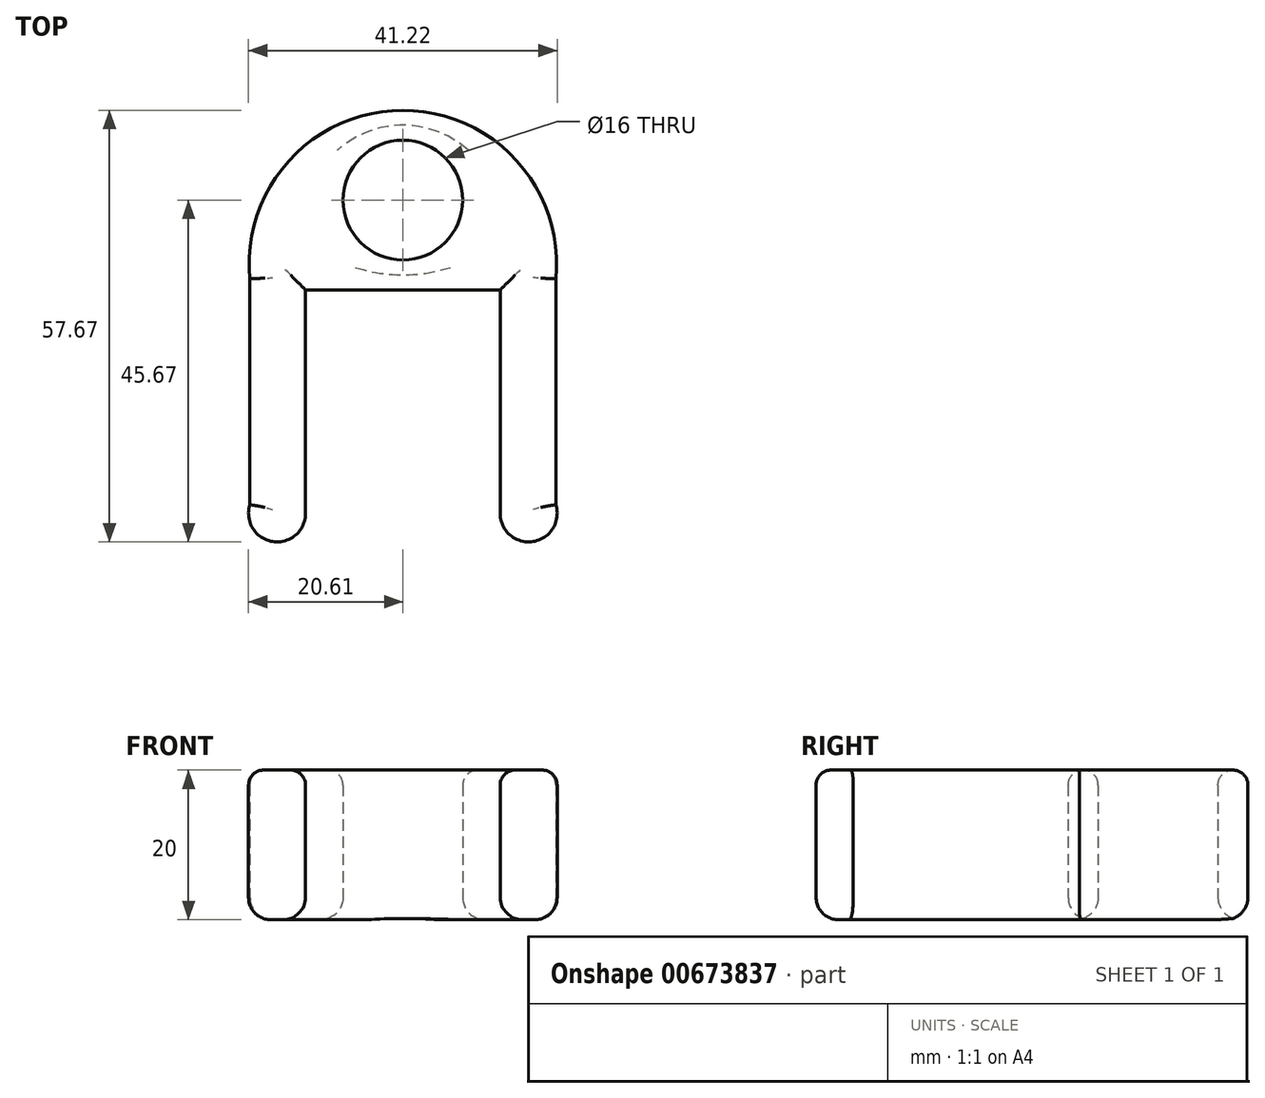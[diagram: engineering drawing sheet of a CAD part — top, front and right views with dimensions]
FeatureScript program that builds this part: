
annotation { "Feature Type Name" : "Feature", "Feature Type Description" : "" }
export const myFeature = defineFeature(function(context is Context, id is Id, definition is map)
    precondition{}
    {
        {
            var Q0;
            Q0=qCreatedBy(makeId("Top.planeOp"),FACE);
            var sketch = newSketch(context, id + "F0", { "sketchPlane" : qUnion([Q0])});
            skCircle(sketch, "E0", {"center": v(0, 0) * mm, "radius": 8 * mm});
            skArc(sketch, "E1", {"start": v(20.42, -10.53) * mm, "mid": v(0, 12) * mm, "end": v(-20.42, -10.53) * mm});
            skLineSegment(sketch, "E2", {"start": v(20.42, -10.53) * mm, "end": v(20.42, -40.7) * mm});
            skLineSegment(sketch, "E3", {"start": v(13, -12) * mm, "end": v(13, -41.87) * mm});
            skLineSegment(sketch, "E4.MirrorCS", {"start": v(-13, -12) * mm, "end": v(-13, -41.87) * mm});
            skLineSegment(sketch, "E5.MirrorCS", {"start": v(-20.42, -10.53) * mm, "end": v(-20.42, -40.7) * mm});
            skArc(sketch, "E6", {"start": v(13, -41.87) * mm, "mid": v(17.4, -45.63) * mm, "end": v(20.42, -40.7) * mm});
            skArc(sketch, "E7.MirrorCS", {"start": v(-13, -41.87) * mm, "mid": v(-17.4, -45.63) * mm, "end": v(-20.42, -40.7) * mm});
            skLineSegment(sketch, "E8", {"start": v(-13, -12) * mm, "end": v(13, -12) * mm});
            skSolve(sketch);
        }
        {
            var Q0;
            Q0=makeQuery(id+"F0.imprint","IMPRINT",FACE,{"disambiguationData":[TD([[makeQuery(id+"F0.imprint","IMPRINT",EDGE,{"derivedFrom":sQuery(id+"F0.wireOp",EDGE,"E0")}),-1.0]])]});
            extrude(context, id + "F1", {"entities" : qUnion([Q0]), "depth" : 20 * mm, "offsetDistance" : 25 * mm});
        }
        {
            var Q0;
            Q0=makeQuery(id+"F1.opExtrude","CAP_EDGE",EDGE,{"disambiguationData":[OSD([sQuery(id+"F0.wireOp",EDGE,"E2")])],"isStart":false});
            var Q1;
            Q1=makeQuery(id+"F1.opExtrude","CAP_EDGE",EDGE,{"disambiguationData":[OSD([sQuery(id+"F0.wireOp",EDGE,"E1")])],"isStart":false});
            var Q2;
            Q2=makeQuery(id+"F1.opExtrude","CAP_EDGE",EDGE,{"disambiguationData":[OSD([sQuery(id+"F0.wireOp",EDGE,"E8")])],"isStart":false});
            var Q3;
            Q3=makeQuery(id+"F1.opExtrude","CAP_EDGE",EDGE,{"disambiguationData":[OSD([sQuery(id+"F0.wireOp",EDGE,"E3")])],"isStart":false});
            var Q4;
            Q4=makeQuery(id+"F1.opExtrude","CAP_EDGE",EDGE,{"disambiguationData":[OSD([sQuery(id+"F0.wireOp",EDGE,"E6")])],"isStart":false});
            var Q5;
            Q5=makeQuery(id+"F1.opExtrude","CAP_EDGE",EDGE,{"disambiguationData":[OSD([sQuery(id+"F0.wireOp",EDGE,"E7.MirrorCS")])],"isStart":false});
            var Q6;
            Q6=makeQuery(id+"F1.opExtrude","CAP_FACE",FACE,{"disambiguationData":[OSD([sQuery(id+"F0.wireOp",EDGE,"E0"),sQuery(id+"F0.wireOp",EDGE,"E1"),sQuery(id+"F0.wireOp",EDGE,"E2"),sQuery(id+"F0.wireOp",EDGE,"E3"),sQuery(id+"F0.wireOp",EDGE,"E4.MirrorCS"),sQuery(id+"F0.wireOp",EDGE,"E5.MirrorCS"),sQuery(id+"F0.wireOp",EDGE,"E6"),sQuery(id+"F0.wireOp",EDGE,"E7.MirrorCS"),sQuery(id+"F0.wireOp",EDGE,"E8")])],"isStart":false});
            fillet(context, id + "F2", {"entities" : qUnion([Q0, Q1, Q2, Q3, Q4, Q5, Q6]), "radius" : 2 * mm, "tangentPropagation" : true, "allowEdgeOverflow" : false});
        }
        {
            var Q0;
            Q0=makeQuery(id+"F1.opExtrude","CAP_FACE",FACE,{"disambiguationData":[OSD([sQuery(id+"F0.wireOp",EDGE,"E0"),sQuery(id+"F0.wireOp",EDGE,"E1"),sQuery(id+"F0.wireOp",EDGE,"E2"),sQuery(id+"F0.wireOp",EDGE,"E3"),sQuery(id+"F0.wireOp",EDGE,"E4.MirrorCS"),sQuery(id+"F0.wireOp",EDGE,"E5.MirrorCS"),sQuery(id+"F0.wireOp",EDGE,"E6"),sQuery(id+"F0.wireOp",EDGE,"E7.MirrorCS"),sQuery(id+"F0.wireOp",EDGE,"E8")])],"isStart":true});
            fillet(context, id + "F3", {"entities" : qUnion([Q0]), "radius" : 3 * mm, "tangentPropagation" : true, "allowEdgeOverflow" : false});
        }
    });
